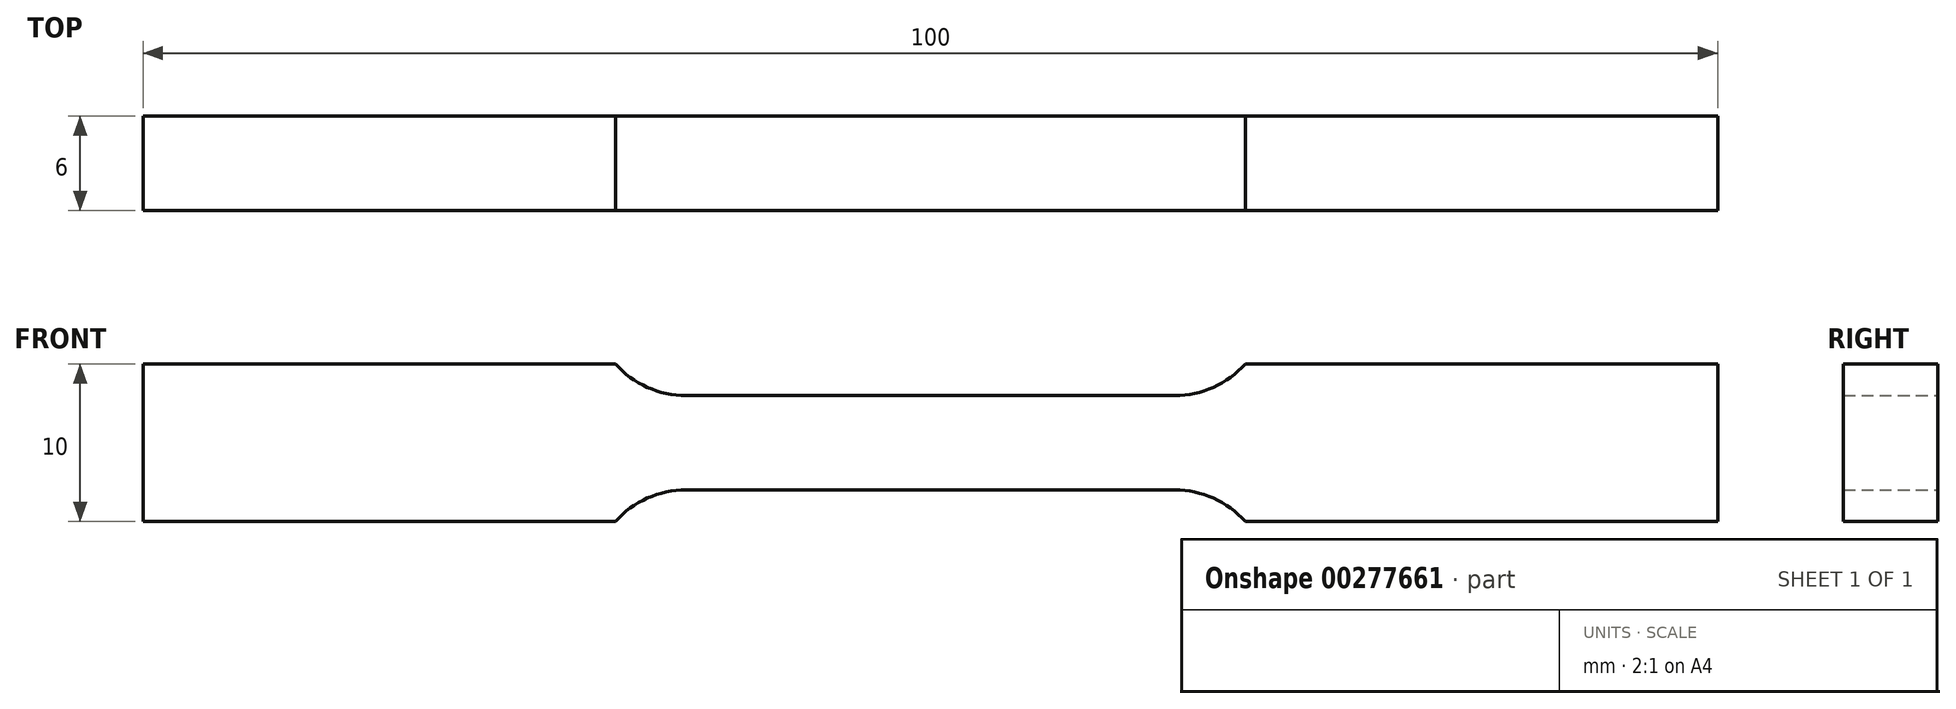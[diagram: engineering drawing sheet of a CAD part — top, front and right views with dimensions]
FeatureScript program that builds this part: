
annotation { "Feature Type Name" : "Feature", "Feature Type Description" : "" }
export const myFeature = defineFeature(function(context is Context, id is Id, definition is map)
    precondition{}
    {
        {
            var Q0;
            Q0=qCreatedBy(makeId("Front.planeOp"),FACE);
            var sketch = newSketch(context, id + "F0", { "sketchPlane" : qUnion([Q0])});
            skLineSegment(sketch, "E0", {"start": v(0, 3) * mm, "end": v(15.53, 3) * mm});
            skArc(sketch, "E1", {"start": v(15.53, 3) * mm, "mid": v(17.98, 3.52) * mm, "end": v(20, 5) * mm});
            skLineSegment(sketch, "E2", {"start": v(20, 5) * mm, "end": v(50, 5) * mm});
            skLineSegment(sketch, "E3", {"start": v(50, 5) * mm, "end": v(50, 0) * mm});
            skLineSegment(sketch, "E4.MirrorCS", {"start": v(0, -3) * mm, "end": v(15.53, -3) * mm});
            skLineSegment(sketch, "E5.MirrorCS", {"start": v(50, -5) * mm, "end": v(50, 0) * mm});
            skLineSegment(sketch, "E6.MirrorCS", {"start": v(20, -5) * mm, "end": v(50, -5) * mm});
            skArc(sketch, "E7.MirrorCS", {"start": v(15.53, -3) * mm, "mid": v(17.98, -3.52) * mm, "end": v(20, -5) * mm});
            skArc(sketch, "E8.MirrorCS", {"start": v(-15.53, -3) * mm, "mid": v(-17.98, -3.52) * mm, "end": v(-20, -5) * mm});
            skLineSegment(sketch, "E9.MirrorCS", {"start": v(-20, -5) * mm, "end": v(-50, -5) * mm});
            skArc(sketch, "E10.MirrorCS", {"start": v(-15.53, 3) * mm, "mid": v(-17.98, 3.52) * mm, "end": v(-20, 5) * mm});
            skLineSegment(sketch, "E11.MirrorCS", {"start": v(-20, 5) * mm, "end": v(-50, 5) * mm});
            skLineSegment(sketch, "E12.MirrorCS", {"start": v(-50, -5) * mm, "end": v(-50, 0) * mm});
            skLineSegment(sketch, "E13.MirrorCS", {"start": v(0, -3) * mm, "end": v(-15.53, -3) * mm});
            skLineSegment(sketch, "E14.MirrorCS", {"start": v(-50, 5) * mm, "end": v(-50, 0) * mm});
            skLineSegment(sketch, "E15.MirrorCS", {"start": v(0, 3) * mm, "end": v(-15.53, 3) * mm});
            skSolve(sketch);
        }
        {
            var Q0;
            Q0 = qSketchRegion(id + "F0", true);
            extrude(context, id + "F1", {"entities" : qUnion([Q0]), "endBound" : BoundingType.SYMMETRIC, "depth" : 6 * mm});
        }
    });
